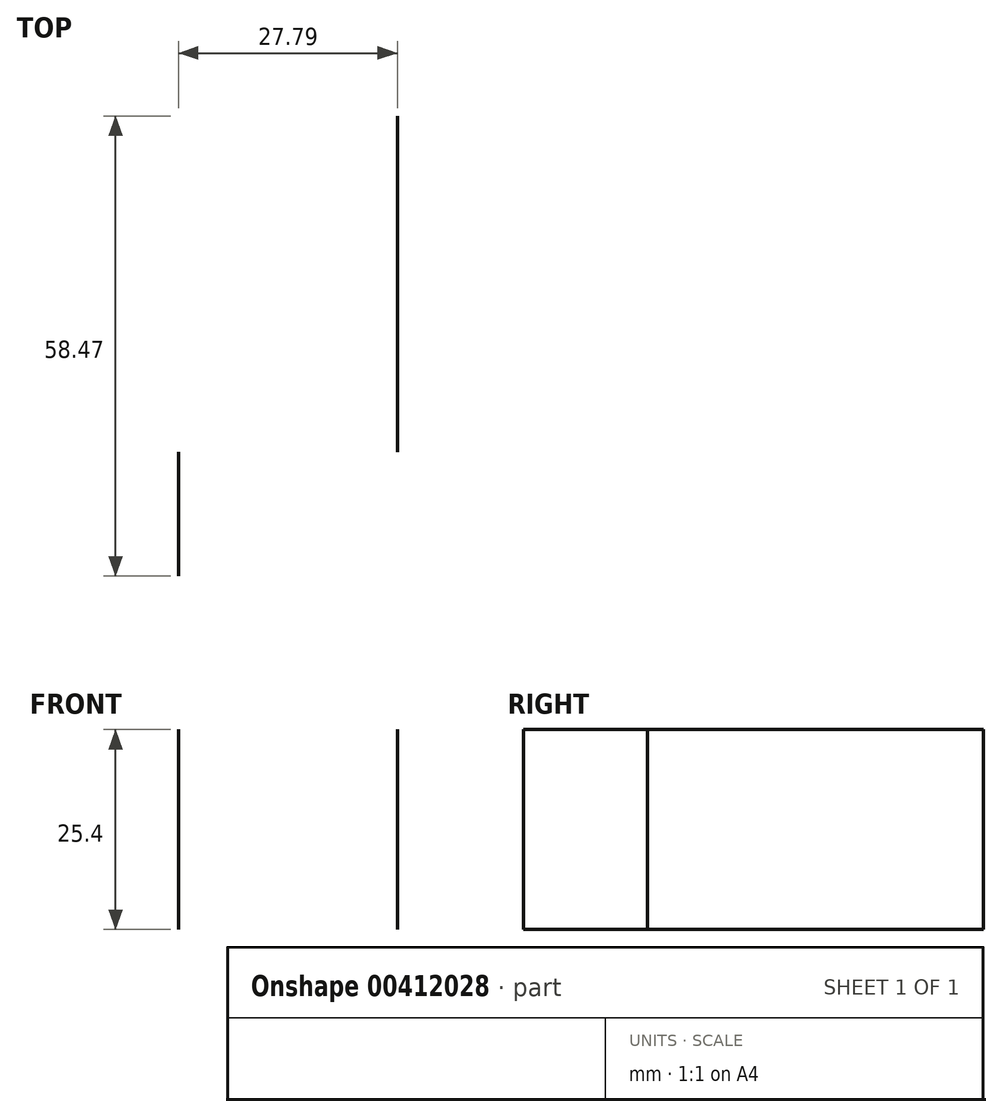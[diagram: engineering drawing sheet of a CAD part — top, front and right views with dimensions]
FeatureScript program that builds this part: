
annotation { "Feature Type Name" : "Feature", "Feature Type Description" : "" }
export const myFeature = defineFeature(function(context is Context, id is Id, definition is map)
    precondition{}
    {
        {
            var Q0;
            Q0=qCreatedBy(makeId("Top.planeOp"),FACE);
            var sketch = newSketch(context, id + "F0", { "sketchPlane" : qUnion([Q0])});
            skLineSegment(sketch, "E0", {"start": v(37.63, 0) * mm, "end": v(0, 0) * mm, "construction": true});
            skLineSegment(sketch, "E1", {"start": v(0, 0) * mm, "end": v(0, -58.47) * mm});
            skLineSegment(sketch, "E2", {"start": v(0, -58.47) * mm, "end": v(28.45, -58.47) * mm});
            skLineSegment(sketch, "E3", {"start": v(28.45, -58.47) * mm, "end": v(28.45, -42.71) * mm});
            skLineSegment(sketch, "E4", {"start": v(28.45, -42.71) * mm, "end": v(56.24, -42.71) * mm});
            skLineSegment(sketch, "E5", {"start": v(56.24, -42.71) * mm, "end": v(56.24, 0) * mm});
            skLineSegment(sketch, "E6", {"start": v(56.24, 0) * mm, "end": v(37.63, 0) * mm});
            skSolve(sketch);
        }
        {
            var Q0;
            Q0=sQuery(id+"F0.wireOp",EDGE,"E3");
            var Q1;
            Q1=sQuery(id+"F0.wireOp",EDGE,"E5");
            extrude(context, id + "F1", {"bodyType" : ToolBodyType.SURFACE, "surfaceEntities" : qUnion([Q0, Q1]), "depth" : 25.4 * mm});
        }
    });
